# Revit family: Water_Heaters_HAJDU_AQUASTIC-AQ-IDE-F_
name_source: partatom
category: Mechanical Equipment
units: mm (PartAtom-declared; Revit-internal decimal feet)

## family parameters
Classification = None
Cut with Voids When Loaded = No
Host = Face
Maintain Annotation Orientation = No
OmniClass Number = 23.31.29.13
OmniClass Title = Hot Water Tank Heaters
Part Type = Normal
Room Calculation Point = No
Round Connector Dimension = Use Diameter
Shared = No

## types (1)
- Nem típus - Terheléstípus katalógus!
    Církulációs csonk = 19.5 mm  [stored 0.0639764 ft]
    Default Elevation = 1219.2 mm  [stored 4 ft]
    Description = Az indirekt fűtésű forróvíztároló tartályában található hőcserélő csőkígyó fűti fel a tartályban lévő használati melegvizet. Falra szerelhető: F változatok elektromos fűtőtesttel ellátott, falra szerelhető indirekt fűtésű forróvíztárolók. Az elektromos fűtőbetéttel ellátott típusok előnye, hogy használati melegvizet biztosítanak kazán vagy napkollektor nélkül is. A kazán vagy napkollektor fűtés vezérlésére és a tárolt víz hőmérsékletének beállítására egy szabályozó szolgál.
    Elektromos futés teljesítmény = 2400 W
    Elektromos pótfűtés = Beépített
    Energiahatékonysági osztály = C
    Felfogatási pontmagasság = 500 mm  [stored 1.64042 ft]
    Felfutési ido elektromos futovel = 1.9 h
    Feszültség = 230 V
    Frekvencia = 50 Hz
    Fázisok száma = 1
    Hocserélo felulete = 0.615 m2
    Hocserélo névleges urtartalma = 4.3 l
    Hocserélo tartós teljesítmény = 18.5 kW
    Házház anyaga = Hajdu - Felület - Fehér
    Korrózióvédelem = tűzzománc + aktív anód
    Látszólagos terhelés = 2530 VA
    Magasság = 750 mm  [stored 2.46063 ft]
    Magasság "B" = 260 mm  [stored 0.853018 ft]
    Magasság "M" = 670 mm  [stored 2.19816 ft]
    Manufacturer = HAJDU
    Max. vízhomérséklet = 65 °C
    Model = Modell nincs megadva - Terheléstípus katalógus!
    Névleges urtartalom = 75 l
    Product Page URL = https://hajdurt.hu
    Tartos teljesítmény = 450 liter/h
    Teljesítménytényezo = 1
    Tárolási veszteség = 48 W
    Tömeg = 39.00 kg
    URL = https://hajdurt.hu
    Vízcsatlakozás = 25.4 mm  [stored 0.0833333 ft]
    Áramfelvétel = 11 A
    Átméro = 515 mm  [stored 1.68963 ft]
    Érintésvédelmi osztály = I.
    Érzékelo tokcso = 11 mm  [stored 0.0360892 ft]
    Üzemi nyomás = 0.6 MPa

note: [stored X ft] marks values corroborated as IEEE doubles in the binary element streams (Revit-internal decimal feet)

## geometry (parser evidence)
native form markers: Sweep x8
no freeform markers — native parametric forms only
